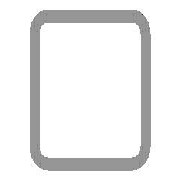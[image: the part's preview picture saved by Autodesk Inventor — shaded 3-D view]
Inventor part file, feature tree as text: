
AUTODESK INVENTOR PART (.ipt)
format: ipt  version: 2022.1 (Build 261234000, 234)  size: 137,216 bytes
history: native  units: mm (DEFAULTED — no unit token found)
features: other x3, sketch x3, extrude x1, plane x1
ambient origin geometry x8: Origin, YZ Plane, XZ Plane, XY Plane, X Axis, Y Axis, Z Axis, Center Point
bodies: Solid1 (feature_tree)
feature tree (8):
  other  "Driven Length"
  other  "Plano inicial"
  other  "Plano final"
  extrude  "Cuerpo"  Depth=20.0mm
  sketch  "Boceto1"  dims[d4=0.0mm d8=20.0mm]
  sketch  "Sketch2"  dims[d9=20.0mm]
  plane  "Work Plane3"
  sketch  "Sketch3"  dims[d10=4.0mm d11=-0.0mm d12=1550.0mm d13=90.0deg d14=1550.0mm]
